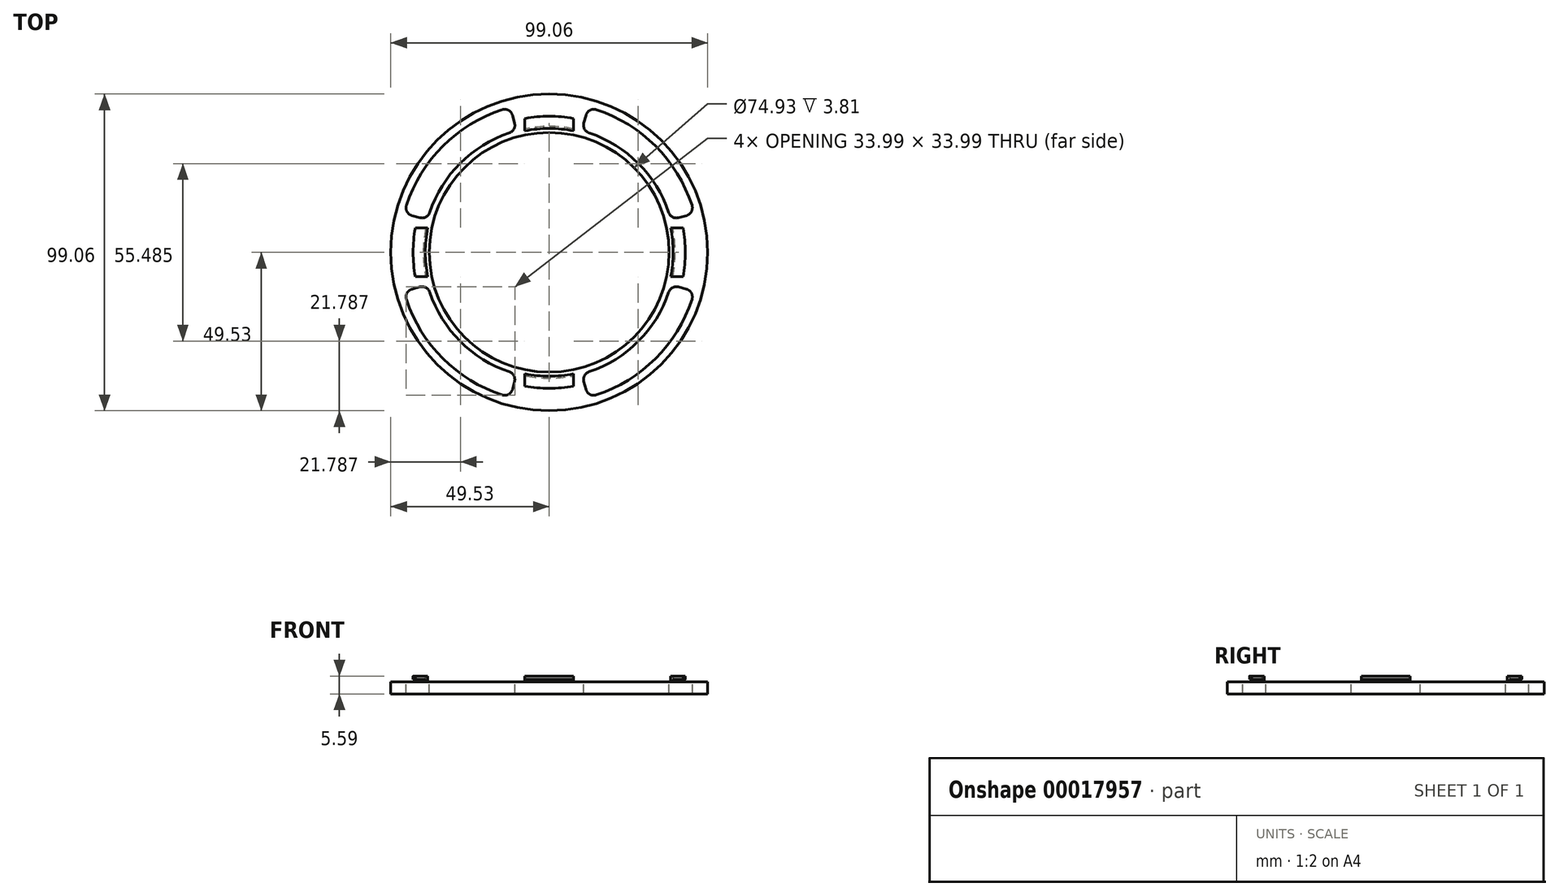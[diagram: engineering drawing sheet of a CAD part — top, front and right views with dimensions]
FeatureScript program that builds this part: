
annotation { "Feature Type Name" : "Feature", "Feature Type Description" : "" }
export const myFeature = defineFeature(function(context is Context, id is Id, definition is map)
    precondition{}
    {
        {
            var Q0;
            Q0=qCreatedBy(makeId("Top.planeOp"),FACE);
            var sketch = newSketch(context, id + "F0", { "sketchPlane" : qUnion([Q0])});
            skArc(sketch, "E0", {"start": v(7.62, 37.98) * mm, "mid": v(0, 38.73) * mm, "end": v(-7.62, 37.98) * mm});
            skArc(sketch, "E1", {"start": v(7.62, 38.63) * mm, "mid": v(0, 39.37) * mm, "end": v(-7.62, 38.63) * mm});
            skLineSegment(sketch, "E2.left", {"start": v(7.62, 38.63) * mm, "end": v(7.62, 37.98) * mm});
            skLineSegment(sketch, "E2.right", {"start": v(-7.62, 38.63) * mm, "end": v(-7.62, 37.98) * mm});
            skLineSegment(sketch, "E3.bottom", {"start": v(-38.63, 7.62) * mm, "end": v(-37.98, 7.62) * mm});
            skLineSegment(sketch, "E3.top", {"start": v(-38.63, -7.62) * mm, "end": v(-37.98, -7.62) * mm});
            skPoint(sketch, "E2.bottom.end.orphan", {"position": v(-7.62, 58.13) * mm});
            skPoint(sketch, "E4.orphan", {"position": v(7.62, 58.13) * mm});
            skArc(sketch, "E5.trimOffspring", {"start": v(-37.98, 7.62) * mm, "mid": v(-38.73, 0) * mm, "end": v(-37.98, -7.62) * mm});
            skArc(sketch, "E6.trimOffspring", {"start": v(-38.63, 7.62) * mm, "mid": v(-39.37, 0) * mm, "end": v(-38.63, -7.62) * mm});
            skPoint(sketch, "E3.left.end.orphan", {"position": v(-62.75, -7.62) * mm});
            skPoint(sketch, "E3.left.start.orphan", {"position": v(-62.75, 7.62) * mm});
            skLineSegment(sketch, "E7.trimOffspring", {"start": v(37.98, -7.62) * mm, "end": v(38.63, -7.62) * mm});
            skLineSegment(sketch, "E8.trimOffspring", {"start": v(37.98, 7.62) * mm, "end": v(38.63, 7.62) * mm});
            skArc(sketch, "E9.trimOffspring", {"start": v(-7.62, -37.98) * mm, "mid": v(0, -38.73) * mm, "end": v(7.62, -37.98) * mm});
            skArc(sketch, "E10.trimOffspring", {"start": v(-7.05, -38.73) * mm, "mid": v(0, -39.37) * mm, "end": v(7.05, -38.73) * mm});
            skArc(sketch, "E11.trimOffspring", {"start": v(37.98, -7.62) * mm, "mid": v(38.73, 0) * mm, "end": v(37.98, 7.62) * mm});
            skArc(sketch, "E12.trimOffspring", {"start": v(38.63, -7.62) * mm, "mid": v(39.37, 0) * mm, "end": v(38.63, 7.62) * mm});
            skPoint(sketch, "E2.top.end.orphan", {"position": v(-7.62, -58.13) * mm});
            skPoint(sketch, "E2.top.start.orphan", {"position": v(7.62, -58.13) * mm});
            skLineSegment(sketch, "E13.trimOffspring", {"start": v(7.62, -37.98) * mm, "end": v(7.05, -38.73) * mm});
            skLineSegment(sketch, "E14.trimOffspring", {"start": v(-7.62, -37.98) * mm, "end": v(-7.05, -38.73) * mm});
            skPoint(sketch, "E3.right.start.orphan", {"position": v(62.75, 7.62) * mm});
            skPoint(sketch, "E15.orphan", {"position": v(62.75, -7.62) * mm});
            skSolve(sketch);
        }
        {
            var Q0;
            Q0 = qSketchRegion(id + "F0", true);
            extrude(context, id + "F1", {"entities" : qUnion([Q0]), "depth" : 0.76 * mm, "offsetDistance" : 25.4 * mm});
        }
        {
            var Q0;
            Q0=qCreatedBy(makeId("Top.planeOp"),FACE);
            var sketch = newSketch(context, id + "F2", { "sketchPlane" : qUnion([Q0])});
            skCircle(sketch, "E16", {"center": v(0, 0) * mm, "radius": 49.53 * mm});
            skCircle(sketch, "E17", {"center": v(0, 0) * mm, "radius": 37.47 * mm});
            skSolve(sketch);
        }
        {
            var Q0;
            Q0 = qSketchRegion(id + "F2", true);
            extrude(context, id + "F3", {"entities" : qUnion([Q0]), "operationType" : NewBodyOperationType.ADD, "oppositeDirection" : true, "depth" : 3.8 * mm, "offsetDistance" : 25.4 * mm});
        }
        {
            var Q0;
            Q0=makeQuery(id+"F1.opExtrude","CAP_FACE",FACE,{"disambiguationData":[OSD([sQuery(id+"F0.wireOp",EDGE,"E0"),sQuery(id+"F0.wireOp",EDGE,"E1"),sQuery(id+"F0.wireOp",EDGE,"E2.left"),sQuery(id+"F0.wireOp",EDGE,"E2.right")])],"isStart":false});
            var sketch = newSketch(context, id + "F4", { "sketchPlane" : qUnion([Q0])});
            skArc(sketch, "E18", {"start": v(-41.86, 7.62) * mm, "mid": v(-42.55, 0) * mm, "end": v(-41.86, -7.62) * mm});
            skArc(sketch, "E19", {"start": v(-37.98, 7.62) * mm, "mid": v(-38.73, 0) * mm, "end": v(-37.98, -7.62) * mm});
            skLineSegment(sketch, "E20.left", {"start": v(7.62, 41.86) * mm, "end": v(7.62, 37.98) * mm});
            skLineSegment(sketch, "E20.right", {"start": v(-7.62, 41.86) * mm, "end": v(-7.62, 37.98) * mm});
            skLineSegment(sketch, "E21.bottom", {"start": v(41.86, 7.62) * mm, "end": v(37.98, 7.62) * mm});
            skLineSegment(sketch, "E21.top", {"start": v(41.86, -7.62) * mm, "end": v(37.98, -7.62) * mm});
            skPoint(sketch, "E22.orphan", {"position": v(-7.62, 46.54) * mm});
            skPoint(sketch, "E23.orphan", {"position": v(7.62, 46.54) * mm});
            skLineSegment(sketch, "E24.trimOffspring", {"start": v(7.62, -37.98) * mm, "end": v(7.62, -41.86) * mm});
            skLineSegment(sketch, "E25.trimOffspring", {"start": v(-7.62, -37.98) * mm, "end": v(-7.62, -41.86) * mm});
            skArc(sketch, "E26.trimOffspring", {"start": v(7.62, 41.86) * mm, "mid": v(0, 42.55) * mm, "end": v(-7.62, 41.86) * mm});
            skArc(sketch, "E27.trimOffspring", {"start": v(7.62, 37.98) * mm, "mid": v(0, 38.73) * mm, "end": v(-7.62, 37.98) * mm});
            skLineSegment(sketch, "E28.trimOffspring", {"start": v(-37.98, 7.62) * mm, "end": v(-41.86, 7.62) * mm});
            skLineSegment(sketch, "E29.trimOffspring", {"start": v(-37.98, -7.62) * mm, "end": v(-41.86, -7.62) * mm});
            skPoint(sketch, "E21.right.start.orphan", {"position": v(-50.68, 7.62) * mm});
            skPoint(sketch, "E30.orphan", {"position": v(-50.68, -7.62) * mm});
            skArc(sketch, "E31.trimOffspring", {"start": v(-7.62, -37.98) * mm, "mid": v(0, -38.73) * mm, "end": v(7.62, -37.98) * mm});
            skArc(sketch, "E32.trimOffspring", {"start": v(-7.62, -41.86) * mm, "mid": v(0, -42.55) * mm, "end": v(7.62, -41.86) * mm});
            skArc(sketch, "E33.trimOffspring", {"start": v(41.86, -7.62) * mm, "mid": v(42.55, 0) * mm, "end": v(41.86, 7.62) * mm});
            skArc(sketch, "E34.trimOffspring", {"start": v(37.98, -7.62) * mm, "mid": v(38.73, 0) * mm, "end": v(37.98, 7.62) * mm});
            skPoint(sketch, "E35.orphan", {"position": v(7.62, -46.54) * mm});
            skPoint(sketch, "E36.orphan", {"position": v(-7.62, -46.54) * mm});
            skPoint(sketch, "E21.left.start.orphan", {"position": v(50.68, 7.62) * mm});
            skPoint(sketch, "E37.orphan", {"position": v(50.68, -7.62) * mm});
            skSolve(sketch);
        }
        {
            var Q0;
            Q0 = qSketchRegion(id + "F4", true);
            extrude(context, id + "F5", {"entities" : qUnion([Q0]), "operationType" : NewBodyOperationType.ADD, "depth" : 1.02 * mm, "offsetDistance" : 25.4 * mm});
        }
        {
            var Q0;
            Q0=makeQuery(id+"F3.opExtrude","CAP_FACE",FACE,{"disambiguationData":[OSD([sQuery(id+"F2.wireOp",EDGE,"E16"),sQuery(id+"F2.wireOp",EDGE,"E17")])],"isStart":true});
            var sketch = newSketch(context, id + "F6", { "sketchPlane" : qUnion([Q0])});
            skArc(sketch, "E38", {"start": v(-38.03, -10.19) * mm, "mid": v(-27.84, -27.84) * mm, "end": v(-10.19, -38.03) * mm});
            skArc(sketch, "E39", {"start": v(-45.39, -12.16) * mm, "mid": v(-33.23, -33.23) * mm, "end": v(-12.16, -45.39) * mm});
            skLineSegment(sketch, "E40", {"start": v(-45.39, 12.16) * mm, "end": v(-38.03, 10.19) * mm});
            skLineSegment(sketch, "E41", {"start": v(-10.19, 38.03) * mm, "end": v(-12.16, 45.39) * mm});
            skLineSegment(sketch, "E42", {"start": v(12.16, 45.39) * mm, "end": v(10.19, 38.03) * mm});
            skLineSegment(sketch, "E43", {"start": v(45.39, -12.16) * mm, "end": v(38.03, -10.19) * mm});
            skLineSegment(sketch, "E44", {"start": v(10.19, -38.03) * mm, "end": v(12.16, -45.39) * mm});
            skLineSegment(sketch, "E45", {"start": v(-10.19, -38.03) * mm, "end": v(-12.16, -45.39) * mm});
            skLineSegment(sketch, "E46", {"start": v(-38.03, -10.19) * mm, "end": v(-45.39, -12.16) * mm});
            skLineSegment(sketch, "E47", {"start": v(38.03, 10.19) * mm, "end": v(45.39, 12.16) * mm});
            skArc(sketch, "E48.trimOffspring", {"start": v(10.19, -38.03) * mm, "mid": v(27.84, -27.84) * mm, "end": v(38.03, -10.19) * mm});
            skArc(sketch, "E49.trimOffspring", {"start": v(12.16, -45.39) * mm, "mid": v(33.23, -33.23) * mm, "end": v(45.39, -12.16) * mm});
            skArc(sketch, "E50.trimOffspring", {"start": v(45.39, 12.16) * mm, "mid": v(33.23, 33.23) * mm, "end": v(12.16, 45.39) * mm});
            skArc(sketch, "E51.trimOffspring", {"start": v(38.03, 10.19) * mm, "mid": v(27.84, 27.84) * mm, "end": v(10.19, 38.03) * mm});
            skArc(sketch, "E52.trimOffspring", {"start": v(-10.19, 38.03) * mm, "mid": v(-27.84, 27.84) * mm, "end": v(-38.03, 10.19) * mm});
            skArc(sketch, "E53.trimOffspring", {"start": v(-12.16, 45.39) * mm, "mid": v(-33.23, 33.23) * mm, "end": v(-45.39, 12.16) * mm});
            skSolve(sketch);
        }
        {
            var Q0;
            Q0 = qSketchRegion(id + "F6", true);
            extrude(context, id + "F7", {"entities" : qUnion([Q0]), "operationType" : NewBodyOperationType.REMOVE, "oppositeDirection" : true, "depth" : 25.4 * mm, "offsetDistance" : 25.4 * mm});
        }
        {
            var Q0;
            Q0=makeQuery(id+"F7.boolean.opBoolean","COPY",EDGE,{"derivedFrom":makeQuery(id+"F7.opExtrude","SWEPT_EDGE",EDGE,{"disambiguationData":[OSD([sQuery(id+"F6.wireOp",EDGE,"E41"),sQuery(id+"F6.wireOp",EDGE,"E53.trimOffspring")])]})});
            var Q1;
            Q1=makeQuery(id+"F7.boolean.opBoolean","COPY",EDGE,{"derivedFrom":makeQuery(id+"F7.opExtrude","SWEPT_EDGE",EDGE,{"disambiguationData":[OSD([sQuery(id+"F6.wireOp",EDGE,"E41"),sQuery(id+"F6.wireOp",EDGE,"E52.trimOffspring")])]})});
            var Q2;
            Q2=makeQuery(id+"F7.boolean.opBoolean","COPY",EDGE,{"derivedFrom":makeQuery(id+"F7.opExtrude","SWEPT_EDGE",EDGE,{"disambiguationData":[OSD([sQuery(id+"F6.wireOp",EDGE,"E47"),sQuery(id+"F6.wireOp",EDGE,"E50.trimOffspring")])]})});
            var Q3;
            Q3=makeQuery(id+"F7.boolean.opBoolean","COPY",EDGE,{"derivedFrom":makeQuery(id+"F7.opExtrude","SWEPT_EDGE",EDGE,{"disambiguationData":[OSD([sQuery(id+"F6.wireOp",EDGE,"E43"),sQuery(id+"F6.wireOp",EDGE,"E48.trimOffspring")])]})});
            var Q4;
            Q4=makeQuery(id+"F7.boolean.opBoolean","COPY",EDGE,{"derivedFrom":makeQuery(id+"F7.opExtrude","SWEPT_EDGE",EDGE,{"disambiguationData":[OSD([sQuery(id+"F6.wireOp",EDGE,"E42"),sQuery(id+"F6.wireOp",EDGE,"E50.trimOffspring")])]})});
            var Q5;
            Q5=makeQuery(id+"F7.boolean.opBoolean","COPY",EDGE,{"derivedFrom":makeQuery(id+"F7.opExtrude","SWEPT_EDGE",EDGE,{"disambiguationData":[OSD([sQuery(id+"F6.wireOp",EDGE,"E42"),sQuery(id+"F6.wireOp",EDGE,"E51.trimOffspring")])]})});
            var Q6;
            Q6=makeQuery(id+"F7.boolean.opBoolean","COPY",EDGE,{"derivedFrom":makeQuery(id+"F7.opExtrude","SWEPT_EDGE",EDGE,{"disambiguationData":[OSD([sQuery(id+"F6.wireOp",EDGE,"E47"),sQuery(id+"F6.wireOp",EDGE,"E51.trimOffspring")])]})});
            var Q7;
            Q7=makeQuery(id+"F7.boolean.opBoolean","COPY",EDGE,{"derivedFrom":makeQuery(id+"F7.opExtrude","SWEPT_EDGE",EDGE,{"disambiguationData":[OSD([sQuery(id+"F6.wireOp",EDGE,"E40"),sQuery(id+"F6.wireOp",EDGE,"E53.trimOffspring")])]})});
            var Q8;
            Q8=makeQuery(id+"F7.boolean.opBoolean","COPY",EDGE,{"derivedFrom":makeQuery(id+"F7.opExtrude","SWEPT_EDGE",EDGE,{"disambiguationData":[OSD([sQuery(id+"F6.wireOp",EDGE,"E40"),sQuery(id+"F6.wireOp",EDGE,"E52.trimOffspring")])]})});
            var Q9;
            Q9=makeQuery(id+"F7.boolean.opBoolean","COPY",EDGE,{"derivedFrom":makeQuery(id+"F7.opExtrude","SWEPT_EDGE",EDGE,{"disambiguationData":[OSD([sQuery(id+"F6.wireOp",EDGE,"E39"),sQuery(id+"F6.wireOp",EDGE,"E45")])]})});
            var Q10;
            Q10=makeQuery(id+"F7.boolean.opBoolean","COPY",EDGE,{"derivedFrom":makeQuery(id+"F7.opExtrude","SWEPT_EDGE",EDGE,{"disambiguationData":[OSD([sQuery(id+"F6.wireOp",EDGE,"E38"),sQuery(id+"F6.wireOp",EDGE,"E46")])]})});
            var Q11;
            Q11=makeQuery(id+"F7.boolean.opBoolean","COPY",EDGE,{"derivedFrom":makeQuery(id+"F7.opExtrude","SWEPT_EDGE",EDGE,{"disambiguationData":[OSD([sQuery(id+"F6.wireOp",EDGE,"E39"),sQuery(id+"F6.wireOp",EDGE,"E46")])]})});
            var Q12;
            Q12=makeQuery(id+"F7.boolean.opBoolean","COPY",EDGE,{"derivedFrom":makeQuery(id+"F7.opExtrude","SWEPT_EDGE",EDGE,{"disambiguationData":[OSD([sQuery(id+"F6.wireOp",EDGE,"E38"),sQuery(id+"F6.wireOp",EDGE,"E45")])]})});
            var Q13;
            Q13=makeQuery(id+"F7.boolean.opBoolean","COPY",EDGE,{"derivedFrom":makeQuery(id+"F7.opExtrude","SWEPT_EDGE",EDGE,{"disambiguationData":[OSD([sQuery(id+"F6.wireOp",EDGE,"E43"),sQuery(id+"F6.wireOp",EDGE,"E49.trimOffspring")])]})});
            var Q14;
            Q14=makeQuery(id+"F7.boolean.opBoolean","COPY",EDGE,{"derivedFrom":makeQuery(id+"F7.opExtrude","SWEPT_EDGE",EDGE,{"disambiguationData":[OSD([sQuery(id+"F6.wireOp",EDGE,"E44"),sQuery(id+"F6.wireOp",EDGE,"E48.trimOffspring")])]})});
            var Q15;
            Q15=makeQuery(id+"F7.boolean.opBoolean","COPY",EDGE,{"derivedFrom":makeQuery(id+"F7.opExtrude","SWEPT_EDGE",EDGE,{"disambiguationData":[OSD([sQuery(id+"F6.wireOp",EDGE,"E44"),sQuery(id+"F6.wireOp",EDGE,"E49.trimOffspring")])]})});
            fillet(context, id + "F8", {"entities" : qUnion([Q0, Q1, Q2, Q3, Q4, Q5, Q6, Q7, Q8, Q9, Q10, Q11, Q12, Q13, Q14, Q15]), "tangentPropagation" : true, "radius" : 2.54 * mm, "defaultsChanged" : true, "vertexSettings" : [], "allowEdgeOverflow" : false});
        }
    });
